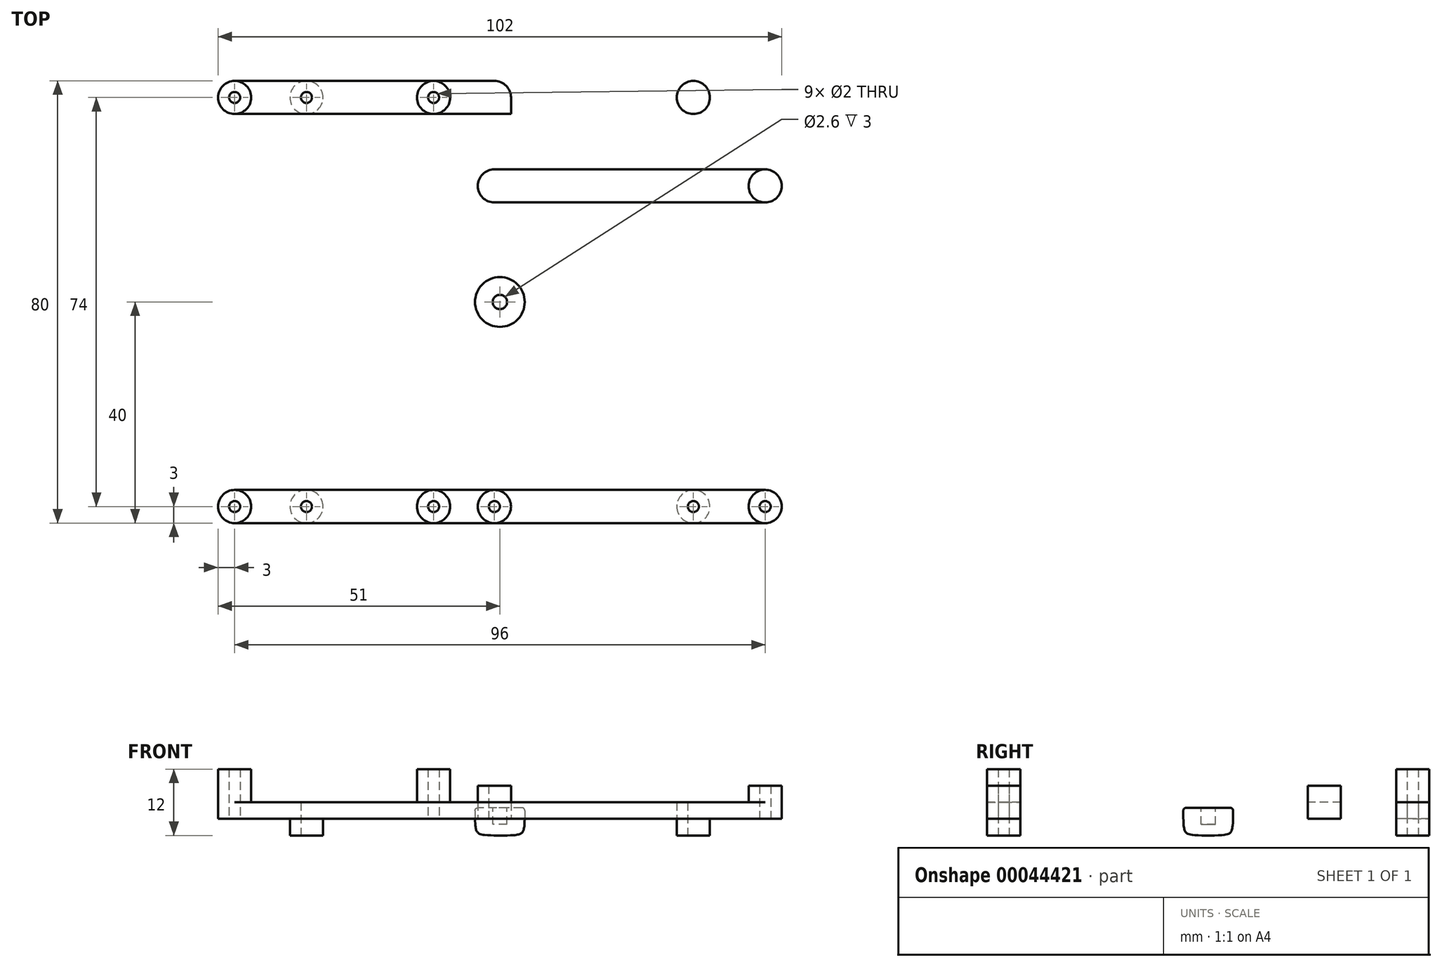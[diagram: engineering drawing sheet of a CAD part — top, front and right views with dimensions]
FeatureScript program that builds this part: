
annotation { "Feature Type Name" : "Feature", "Feature Type Description" : "" }
export const myFeature = defineFeature(function(context is Context, id is Id, definition is map)
    precondition{}
    {
        {
            var Q0;
            Q0=qCreatedBy(makeId("Top.planeOp"),FACE);
            var sketch = newSketch(context, id + "F0", { "sketchPlane" : qUnion([Q0])});
            skPoint(sketch, "E0.rect.middle", {"position": v(0, 0) * mm});
            skPoint(sketch, "E1", {"position": v(-35, 37) * mm});
            skCircle(sketch, "E2", {"center": v(-35, 37) * mm, "radius": 3 * mm});
            skSolve(sketch);
        }
        {
            var Q0;
            Q0=makeQuery(id+"F0.imprint","IMPRINT",FACE,{"disambiguationData":[TD([[makeQuery(id+"F0.imprint","IMPRINT",EDGE,{"derivedFrom":sQuery(id+"F0.wireOp",EDGE,"E2")}),1.0]])]});
            extrude(context, id + "F1", {"entities" : qUnion([Q0]), "depth" : 3 * mm});
        }
        {
            var Q0;
            Q0=makeQuery(id+"F1.opExtrude","SWEPT_BODY",BODY,{"disambiguationData":[OSD([sQuery(id+"F0.wireOp",EDGE,"E2")])]});
            var Q1;
            Q1=qCreatedBy(makeId("Right.planeOp"),FACE);
            mirror(context, id + "F2", {"entities" : qUnion([Q0]), "mirrorPlane" : qUnion([Q1])});
        }
        {
            var Q0;
            Q0=makeQuery(id+"F1.opExtrude","SWEPT_BODY",BODY,{"disambiguationData":[OSD([sQuery(id+"F0.wireOp",EDGE,"E2")])]});
            var Q1;
            Q1=makeQuery(id+"F2.opPattern","COPY",BODY,{"derivedFrom":makeQuery(id+"F1.opExtrude","SWEPT_BODY",BODY,{"disambiguationData":[OSD([sQuery(id+"F0.wireOp",EDGE,"E2")])]}),"instanceName":"1"});
            var Q2;
            Q2=qCreatedBy(makeId("Front.planeOp"),FACE);
            mirror(context, id + "F3", {"entities" : qUnion([Q0, Q1]), "mirrorPlane" : qUnion([Q2])});
        }
        {
            var Q0;
            Q0=makeQuery(id+"F3.opPattern","COPY",FACE,{"derivedFrom":makeQuery(id+"F1.opExtrude","CAP_FACE",FACE,{"disambiguationData":[OSD([sQuery(id+"F0.wireOp",EDGE,"E2")])],"isStart":false}),"instanceName":"1"});
            var sketch = newSketch(context, id + "F4", { "sketchPlane" : qUnion([Q0])});
            skCircle(sketch, "E3.0", {"center": v(-35, -37) * mm, "radius": 3 * mm});
            skCircle(sketch, "E3.1", {"center": v(35, -37) * mm, "radius": 3 * mm});
            skLineSegment(sketch, "E4.bottom", {"start": v(-51, -34) * mm, "end": v(51, -34) * mm});
            skLineSegment(sketch, "E4.top", {"start": v(-51, -40) * mm, "end": v(51, -40) * mm});
            skLineSegment(sketch, "E4.left", {"start": v(-51, -34) * mm, "end": v(-51, -40) * mm});
            skLineSegment(sketch, "E4.right", {"start": v(51, -34) * mm, "end": v(51, -40) * mm});
            skPoint(sketch, "E5", {"position": v(0, -34) * mm});
            skPoint(sketch, "E6", {"position": v(-51, -37) * mm});
            skLineSegment(sketch, "E7.bottom", {"start": v(-51, 40) * mm, "end": v(51, 40) * mm});
            skLineSegment(sketch, "E7.top", {"start": v(-51, 34) * mm, "end": v(51, 34) * mm});
            skLineSegment(sketch, "E7.left", {"start": v(-51, 40) * mm, "end": v(-51, 34) * mm});
            skLineSegment(sketch, "E7.right", {"start": v(51, 40) * mm, "end": v(51, 34) * mm});
            skPoint(sketch, "E8", {"position": v(-51, 37) * mm});
            skPoint(sketch, "E9", {"position": v(0, 40) * mm});
            skCircle(sketch, "E10.0", {"center": v(-35, 37) * mm, "radius": 3 * mm});
            skLineSegment(sketch, "E11.bottom", {"start": v(-51, 40) * mm, "end": v(2, 40) * mm});
            skLineSegment(sketch, "E11.top", {"start": v(-51, 34) * mm, "end": v(2, 34) * mm});
            skLineSegment(sketch, "E11.right", {"start": v(2, 40) * mm, "end": v(2, 34) * mm});
            skLineSegment(sketch, "E12.bottom", {"start": v(2, 34) * mm, "end": v(-4, 34) * mm});
            skLineSegment(sketch, "E12.top", {"start": v(2, 24) * mm, "end": v(-4, 24) * mm});
            skLineSegment(sketch, "E12.left", {"start": v(2, 34) * mm, "end": v(2, 24) * mm});
            skLineSegment(sketch, "E12.right", {"start": v(-4, 34) * mm, "end": v(-4, 24) * mm});
            skLineSegment(sketch, "E13.bottom", {"start": v(-4, 24) * mm, "end": v(51, 24) * mm});
            skLineSegment(sketch, "E13.top", {"start": v(-4, 18) * mm, "end": v(51, 18) * mm});
            skLineSegment(sketch, "E13.left", {"start": v(-4, 24) * mm, "end": v(-4, 18) * mm});
            skLineSegment(sketch, "E13.right", {"start": v(51, 24) * mm, "end": v(51, 18) * mm});
            skLineSegment(sketch, "E14.bottom", {"start": v(32, 40) * mm, "end": v(38, 40) * mm});
            skLineSegment(sketch, "E14.top", {"start": v(32, 24) * mm, "end": v(38, 24) * mm});
            skLineSegment(sketch, "E14.left", {"start": v(32, 40) * mm, "end": v(32, 24) * mm});
            skLineSegment(sketch, "E14.right", {"start": v(38, 40) * mm, "end": v(38, 24) * mm});
            skPoint(sketch, "E15", {"position": v(35, 24) * mm});
            skCircle(sketch, "E16.0", {"center": v(35, 37) * mm, "radius": 3 * mm});
            skSolve(sketch);
        }
        {
            var Q0;
            {var subQ5=sQuery(id+"F4.wireOp",EDGE,"E11.right");Q0=makeQuery(id+"F4.imprint","IMPRINT",FACE,{"disambiguationData":[TD([[makeQuery(id+"F4.imprint","IMPRINT",EDGE,{"derivedFrom":subQ5}),-1.0]])]});}
            var Q1;
            {var subQ0=sQuery(id+"F4.wireOp",EDGE,"E10.0");var subQ1=makeQuery(id+"F4.imprint","INTERSECT",VERTEX,{"derivedFrom":[subQ0,sQuery(id+"F4.wireOp",EDGE,"E11.bottom")]});Q1=makeQuery(id+"F4.imprint","IMPRINT",FACE,{"disambiguationData":[TD([[makeQuery(id+"F4.imprint","IMPRINT",EDGE,{"disambiguationData":[TD([[subQ1,-1.0]])],"derivedFrom":subQ0}),1.0]])]});}
            var Q2;
            {var subQ5=sQuery(id+"F4.wireOp",EDGE,"E7.left");Q2=makeQuery(id+"F4.imprint","IMPRINT",FACE,{"disambiguationData":[TD([[makeQuery(id+"F4.imprint","IMPRINT",EDGE,{"derivedFrom":subQ5}),1.0]])]});}
            var Q3;
            Q3=makeQuery(id+"F4.imprint","IMPRINT",FACE,{"disambiguationData":[TD([[makeQuery(id+"F4.imprint","IMPRINT",EDGE,{"derivedFrom":sQuery(id+"F4.wireOp",EDGE,"E12.bottom")}),1.0]])]});
            var Q4;
            Q4=makeQuery(id+"F4.imprint","IMPRINT",FACE,{"disambiguationData":[TD([[makeQuery(id+"F4.imprint","IMPRINT",EDGE,{"derivedFrom":sQuery(id+"F4.wireOp",EDGE,"E13.top")}),1.0]])]});
            var Q5;
            {var subQ1=sQuery(id+"F4.wireOp",EDGE,"E14.top");Q5=makeQuery(id+"F4.imprint","IMPRINT",FACE,{"disambiguationData":[TD([[makeQuery(id+"F4.imprint","IMPRINT",EDGE,{"derivedFrom":subQ1}),1.0]])]});}
            var Q6;
            {var subQ0=sQuery(id+"F4.wireOp",EDGE,"E14.right");var subQ1=sQuery(id+"F4.wireOp",EDGE,"E7.top");var subQ2=makeQuery(id+"F4.imprint","INTERSECT",VERTEX,{"derivedFrom":[subQ1,subQ0]});Q6=makeQuery(id+"F4.imprint","IMPRINT",FACE,{"disambiguationData":[TD([[makeQuery(id+"F4.imprint","IMPRINT",EDGE,{"disambiguationData":[TD([[subQ2,1.0]])],"derivedFrom":subQ1}),1.0]])]});}
            var Q7;
            {var subQ0=sQuery(id+"F4.wireOp",EDGE,"E14.left");var subQ1=sQuery(id+"F4.wireOp",EDGE,"E7.top");var subQ2=makeQuery(id+"F4.imprint","INTERSECT",VERTEX,{"derivedFrom":[subQ1,subQ0]});Q7=makeQuery(id+"F4.imprint","IMPRINT",FACE,{"disambiguationData":[TD([[makeQuery(id+"F4.imprint","IMPRINT",EDGE,{"disambiguationData":[TD([[subQ2,-1.0]])],"derivedFrom":subQ1}),1.0]])]});}
            var Q8;
            {var subQ0=sQuery(id+"F4.wireOp",EDGE,"E16.0");var subQ1=makeQuery(id+"F4.imprint","INTERSECT",VERTEX,{"derivedFrom":[sQuery(id+"F4.wireOp",EDGE,"E14.bottom"),subQ0]});Q8=makeQuery(id+"F4.imprint","IMPRINT",FACE,{"disambiguationData":[TD([[makeQuery(id+"F4.imprint","IMPRINT",EDGE,{"disambiguationData":[TD([[subQ1,1.0]])],"derivedFrom":subQ0}),1.0]])]});}
            extrude(context, id + "F5", {"entities" : qUnion([Q0, Q1, Q2, Q3, Q4, Q5, Q6, Q7, Q8]), "operationType" : NewBodyOperationType.ADD, "depth" : 3 * mm});
        }
        {
            var Q0;
            Q0=makeQuery(id+"F5.opExtrude","SWEPT_EDGE",EDGE,{"disambiguationData":[OSD([sQuery(id+"F4.wireOp",EDGE,"E11.top"),sQuery(id+"F4.wireOp",EDGE,"E7.left")])]});
            var Q1;
            Q1=makeQuery(id+"F5.opExtrude","SWEPT_EDGE",EDGE,{"disambiguationData":[OSD([sQuery(id+"F4.wireOp",EDGE,"E11.bottom"),sQuery(id+"F4.wireOp",EDGE,"E7.left")])]});
            var Q2;
            Q2=makeQuery(id+"F5.opExtrude","SWEPT_EDGE",EDGE,{"disambiguationData":[OSD([sQuery(id+"F4.wireOp",EDGE,"E7.bottom"),sQuery(id+"F4.wireOp",EDGE,"E11.bottom"),sQuery(id+"F4.wireOp",EDGE,"E11.right")])]});
            var Q3;
            Q3=makeQuery(id+"F5.opExtrude","SWEPT_EDGE",EDGE,{"disambiguationData":[OSD([sQuery(id+"F4.wireOp",EDGE,"E13.top"),sQuery(id+"F4.wireOp",EDGE,"E13.left")])]});
            var Q4;
            Q4=makeQuery(id+"F5.opExtrude","SWEPT_EDGE",EDGE,{"disambiguationData":[OSD([sQuery(id+"F4.wireOp",EDGE,"E13.top"),sQuery(id+"F4.wireOp",EDGE,"E13.right")])]});
            var Q5;
            Q5=makeQuery(id+"F5.opExtrude","SWEPT_EDGE",EDGE,{"disambiguationData":[OSD([sQuery(id+"F4.wireOp",EDGE,"E13.bottom"),sQuery(id+"F4.wireOp",EDGE,"E13.right")])]});
            var Q6;
            Q6=makeQuery(id+"F5.opExtrude","SWEPT_EDGE",EDGE,{"disambiguationData":[OSD([sQuery(id+"F4.wireOp",EDGE,"E13.bottom"),sQuery(id+"F4.wireOp",EDGE,"E14.top"),sQuery(id+"F4.wireOp",EDGE,"E14.right")])]});
            var Q7;
            Q7=makeQuery(id+"F5.opExtrude","SWEPT_EDGE",EDGE,{"disambiguationData":[OSD([sQuery(id+"F4.wireOp",EDGE,"E12.left"),sQuery(id+"F4.wireOp",EDGE,"E13.bottom")])]});
            var Q8;
            Q8=makeQuery(id+"F5.opExtrude","SWEPT_EDGE",EDGE,{"disambiguationData":[OSD([sQuery(id+"F4.wireOp",EDGE,"E13.bottom"),sQuery(id+"F4.wireOp",EDGE,"E14.top"),sQuery(id+"F4.wireOp",EDGE,"E14.left")])]});
            var Q9;
            Q9=makeQuery(id+"F5.opExtrude","SWEPT_EDGE",EDGE,{"disambiguationData":[OSD([sQuery(id+"F4.wireOp",EDGE,"E11.top"),sQuery(id+"F4.wireOp",EDGE,"E12.bottom"),sQuery(id+"F4.wireOp",EDGE,"E12.right")])]});
            fillet(context, id + "F6", {"entities" : qUnion([Q0, Q1, Q2, Q3, Q4, Q5, Q6, Q7, Q8, Q9]), "radius" : 3 * mm, "tangentPropagation" : true, "allowEdgeOverflow" : false});
        }
        {
            var Q0;
            {var subQ0=sQuery(id+"F4.wireOp",EDGE,"E4.bottom");var subQ1=sQuery(id+"F4.wireOp",EDGE,"E3.0");var subQ2=makeQuery(id+"F4.imprint","INTERSECT",VERTEX,{"derivedFrom":[subQ1,subQ0]});Q0=makeQuery(id+"F4.imprint","IMPRINT",FACE,{"disambiguationData":[TD([[makeQuery(id+"F4.imprint","IMPRINT",EDGE,{"disambiguationData":[TD([[subQ2,-1.0]])],"derivedFrom":subQ1}),1.0]])]});}
            var Q1;
            Q1=makeQuery(id+"F4.imprint","IMPRINT",FACE,{"disambiguationData":[TD([[makeQuery(id+"F4.imprint","IMPRINT",EDGE,{"derivedFrom":makeQuery(id+"F3.opPattern","COPY",EDGE,{"derivedFrom":makeQuery(id+"Fms3Rmutws8Ll0A_1.hole-0.boolean.opBoolean","INTERSECT",EDGE,{"derivedFrom":[makeQuery(id+"F1.opExtrude","CAP_FACE",FACE,{"disambiguationData":[OSD([sQuery(id+"F0.wireOp",EDGE,"E2")])],"isStart":false}),makeQuery(id+"Fms3Rmutws8Ll0A_1.hole-0.opRevolve","SWEPT_FACE",FACE,{"disambiguationData":[OSD([sQuery(id+"Fms3Rmutws8Ll0A_1.hole-0.sketch.wireOp",EDGE,"core_line_2")])]})]}),"instanceName":"1"})}),-1.0]])]});
            var Q2;
            Q2=makeQuery(id+"F4.imprint","IMPRINT",FACE,{"disambiguationData":[TD([[makeQuery(id+"F4.imprint","IMPRINT",EDGE,{"derivedFrom":makeQuery(id+"F3.opPattern","COPY",EDGE,{"derivedFrom":makeQuery(id+"Fms3Rmutws8Ll0A_1.hole-0.boolean.opBoolean","INTERSECT",EDGE,{"derivedFrom":[makeQuery(id+"F1.opExtrude","CAP_FACE",FACE,{"disambiguationData":[OSD([sQuery(id+"F0.wireOp",EDGE,"E2")])],"isStart":false}),makeQuery(id+"Fms3Rmutws8Ll0A_1.hole-0.opRevolve","SWEPT_FACE",FACE,{"disambiguationData":[OSD([sQuery(id+"Fms3Rmutws8Ll0A_1.hole-0.sketch.wireOp",EDGE,"core_line_2")])]})]}),"instanceName":"1"})}),1.0]])]});
            var Q3;
            {var subQ5=sQuery(id+"F4.wireOp",EDGE,"E4.left");Q3=makeQuery(id+"F4.imprint","IMPRINT",FACE,{"disambiguationData":[TD([[makeQuery(id+"F4.imprint","IMPRINT",EDGE,{"derivedFrom":subQ5}),1.0]])]});}
            var Q4;
            {var subQ5=sQuery(id+"F4.wireOp",EDGE,"E4.right");Q4=makeQuery(id+"F4.imprint","IMPRINT",FACE,{"disambiguationData":[TD([[makeQuery(id+"F4.imprint","IMPRINT",EDGE,{"derivedFrom":subQ5}),-1.0]])]});}
            var Q5;
            {var subQ0=sQuery(id+"F4.wireOp",EDGE,"E3.1");var subQ1=makeQuery(id+"F4.imprint","INTERSECT",VERTEX,{"derivedFrom":[subQ0,sQuery(id+"F4.wireOp",EDGE,"E4.bottom")]});Q5=makeQuery(id+"F4.imprint","IMPRINT",FACE,{"disambiguationData":[TD([[makeQuery(id+"F4.imprint","IMPRINT",EDGE,{"disambiguationData":[TD([[subQ1,-1.0]])],"derivedFrom":subQ0}),1.0]])]});}
            var Q6;
            {var subQ0=sQuery(id+"F4.wireOp",EDGE,"E3.0");var subQ1=makeQuery(id+"F4.imprint","INTERSECT",VERTEX,{"derivedFrom":[subQ0,sQuery(id+"F4.wireOp",EDGE,"E4.bottom")]});Q6=makeQuery(id+"F4.imprint","IMPRINT",FACE,{"disambiguationData":[TD([[makeQuery(id+"F4.imprint","IMPRINT",EDGE,{"disambiguationData":[TD([[subQ1,1.0]])],"derivedFrom":subQ0}),-1.0]])]});}
            extrude(context, id + "F7", {"entities" : qUnion([Q0, Q1, Q2, Q3, Q4, Q5, Q6]), "operationType" : NewBodyOperationType.ADD, "depth" : 3 * mm});
        }
        {
            var Q0;
            Q0=makeQuery(id+"F7.opExtrude","SWEPT_EDGE",EDGE,{"disambiguationData":[OSD([sQuery(id+"F4.wireOp",EDGE,"E4.bottom"),sQuery(id+"F4.wireOp",EDGE,"E4.left")])]});
            var Q1;
            Q1=makeQuery(id+"F7.opExtrude","SWEPT_EDGE",EDGE,{"disambiguationData":[OSD([sQuery(id+"F4.wireOp",EDGE,"E4.top"),sQuery(id+"F4.wireOp",EDGE,"E4.left")])]});
            var Q2;
            Q2=makeQuery(id+"F7.opExtrude","SWEPT_EDGE",EDGE,{"disambiguationData":[OSD([sQuery(id+"F4.wireOp",EDGE,"E4.bottom"),sQuery(id+"F4.wireOp",EDGE,"E4.right")])]});
            var Q3;
            Q3=makeQuery(id+"F7.opExtrude","SWEPT_EDGE",EDGE,{"disambiguationData":[OSD([sQuery(id+"F4.wireOp",EDGE,"E4.top"),sQuery(id+"F4.wireOp",EDGE,"E4.right")])]});
            fillet(context, id + "F8", {"entities" : qUnion([Q0, Q1, Q2, Q3]), "radius" : 3 * mm, "tangentPropagation" : true, "allowEdgeOverflow" : false});
        }
        {
            var Q0;
            Q0=makeQuery(id+"F7.opExtrude","CAP_FACE",FACE,{"disambiguationData":[OSD([sQuery(id+"F4.wireOp",EDGE,"E4.bottom"),sQuery(id+"F4.wireOp",EDGE,"E4.top"),sQuery(id+"F4.wireOp",EDGE,"E4.left"),sQuery(id+"F4.wireOp",EDGE,"E4.right")])],"isStart":false});
            var sketch = newSketch(context, id + "F9", { "sketchPlane" : qUnion([Q0])});
            skArc(sketch, "E17.0", {"start": v(-48, -34) * mm, "mid": v(-51, -37) * mm, "end": v(-48, -40) * mm});
            skCircle(sketch, "E18", {"center": v(-48, -37) * mm, "radius": 3 * mm});
            skCircle(sketch, "E19", {"center": v(-12, -37) * mm, "radius": 3 * mm});
            skArc(sketch, "E20.0", {"start": v(48, -40) * mm, "mid": v(51, -37) * mm, "end": v(48, -34) * mm});
            skCircle(sketch, "E21", {"center": v(48, -37) * mm, "radius": 3 * mm});
            skCircle(sketch, "E22", {"center": v(-1, -37) * mm, "radius": 3 * mm});
            skCircle(sketch, "E23.0", {"center": v(-35, -37) * mm, "radius": 3 * mm});
            skCircle(sketch, "E23.1", {"center": v(35, -37) * mm, "radius": 3 * mm});
            skSolve(sketch);
        }
        {
            var Q0;
            {var subQ0=sQuery(id+"F9.wireOp",EDGE,"E19");var subQ1=makeQuery(id+"F9.imprint","INTERSECT",VERTEX,{"derivedFrom":[makeQuery(id+"F7.opExtrude","CAP_EDGE",EDGE,{"disambiguationData":[OSD([sQuery(id+"F4.wireOp",EDGE,"E4.bottom")])],"isStart":false}),subQ0]});Q0=makeQuery(id+"F9.imprint","IMPRINT",FACE,{"disambiguationData":[TD([[makeQuery(id+"F9.imprint","IMPRINT",EDGE,{"disambiguationData":[TD([[subQ1,-1.0]])],"derivedFrom":subQ0}),1.0]])]});}
            var Q1;
            {var subQ0=sQuery(id+"F9.wireOp",EDGE,"E18");var subQ1=makeQuery(id+"F9.imprint","INTERSECT",VERTEX,{"derivedFrom":[makeQuery(id+"F7.opExtrude","CAP_EDGE",EDGE,{"disambiguationData":[OSD([sQuery(id+"F4.wireOp",EDGE,"E4.bottom")])],"isStart":false}),subQ0]});Q1=makeQuery(id+"F9.imprint","IMPRINT",FACE,{"disambiguationData":[TD([[makeQuery(id+"F9.imprint","IMPRINT",EDGE,{"disambiguationData":[TD([[subQ1,-1.0]])],"derivedFrom":subQ0}),1.0]])]});}
            extrude(context, id + "F10", {"entities" : qUnion([Q0, Q1]), "operationType" : NewBodyOperationType.ADD, "depth" : 6 * mm});
        }
        {
            var Q0;
            {var subQ0=sQuery(id+"F9.wireOp",EDGE,"E22");var subQ1=makeQuery(id+"F9.imprint","INTERSECT",VERTEX,{"derivedFrom":[makeQuery(id+"F7.opExtrude","CAP_EDGE",EDGE,{"disambiguationData":[OSD([sQuery(id+"F4.wireOp",EDGE,"E4.bottom")])],"isStart":false}),subQ0]});Q0=makeQuery(id+"F9.imprint","IMPRINT",FACE,{"disambiguationData":[TD([[makeQuery(id+"F9.imprint","IMPRINT",EDGE,{"disambiguationData":[TD([[subQ1,-1.0]])],"derivedFrom":subQ0}),1.0]])]});}
            var Q1;
            {var subQ0=sQuery(id+"F9.wireOp",EDGE,"E21");var subQ1=makeQuery(id+"F9.imprint","INTERSECT",VERTEX,{"derivedFrom":[makeQuery(id+"F7.opExtrude","CAP_EDGE",EDGE,{"disambiguationData":[OSD([sQuery(id+"F4.wireOp",EDGE,"E4.bottom")])],"isStart":false}),subQ0]});Q1=makeQuery(id+"F9.imprint","IMPRINT",FACE,{"disambiguationData":[TD([[makeQuery(id+"F9.imprint","IMPRINT",EDGE,{"disambiguationData":[TD([[subQ1,-1.0]])],"derivedFrom":subQ0}),1.0]])]});}
            extrude(context, id + "F11", {"entities" : qUnion([Q0, Q1]), "operationType" : NewBodyOperationType.ADD, "depth" : 3 * mm});
        }
        {
            var Q0;
            Q0=makeQuery(id+"F10.opExtrude","CAP_FACE",FACE,{"disambiguationData":[OSD([sQuery(id+"F9.wireOp",EDGE,"E18")])],"isStart":false});
            var sketch = newSketch(context, id + "F12", { "sketchPlane" : qUnion([Q0])});
            skCircle(sketch, "E24.0", {"center": v(-48, -37) * mm, "radius": 3 * mm});
            skCircle(sketch, "E24.1", {"center": v(-12, -37) * mm, "radius": 3 * mm});
            skCircle(sketch, "E24.2", {"center": v(-1, -37) * mm, "radius": 3 * mm});
            skCircle(sketch, "E24.3", {"center": v(48, -37) * mm, "radius": 3 * mm});
            skSolve(sketch);
        }
        {
            var Q0;
            Q0=sQuery(id+"F12.wireOp",VERTEX,"E24.0.center");
            var Q1;
            Q1=sQuery(id+"F12.wireOp",VERTEX,"E24.1.center");
            var Q2;
            Q2=sQuery(id+"F12.wireOp",VERTEX,"E24.2.center");
            var Q3;
            Q3=sQuery(id+"F12.wireOp",VERTEX,"E24.3.center");
            var Q4;
            Q4=makeQuery(id+"F3.opPattern","COPY",BODY,{"derivedFrom":makeQuery(id+"F1.opExtrude","SWEPT_BODY",BODY,{"disambiguationData":[OSD([sQuery(id+"F0.wireOp",EDGE,"E2")])]}),"instanceName":"1"});
            hole(context, id + "F13", {"style" : HoleStyle.SIMPLE, "holeDiameter" : 2 * mm, "endStyle" : HoleEndStyle.THROUGH, "locations" : qUnion([Q0, Q1, Q2, Q3]), "scope" : qUnion([Q4])});
        }
        {
            var Q0;
            Q0=makeQuery(id+"F5.opExtrude","CAP_FACE",FACE,{"disambiguationData":[OSD([sQuery(id+"F4.wireOp",EDGE,"E11.bottom"),sQuery(id+"F4.wireOp",EDGE,"E11.top"),sQuery(id+"F4.wireOp",EDGE,"E7.left"),sQuery(id+"F4.wireOp",EDGE,"E11.right"),sQuery(id+"F4.wireOp",EDGE,"E12.left"),sQuery(id+"F4.wireOp",EDGE,"E12.right"),sQuery(id+"F4.wireOp",EDGE,"E13.bottom"),sQuery(id+"F4.wireOp",EDGE,"E13.top"),sQuery(id+"F4.wireOp",EDGE,"E13.left"),sQuery(id+"F4.wireOp",EDGE,"E13.right"),sQuery(id+"F4.wireOp",EDGE,"E14.left"),sQuery(id+"F4.wireOp",EDGE,"E14.right"),sQuery(id+"F4.wireOp",EDGE,"E16.0")])],"isStart":false});
            var sketch = newSketch(context, id + "F14", { "sketchPlane" : qUnion([Q0])});
            skArc(sketch, "E25.0", {"start": v(-4, 21) * mm, "mid": v(-3.12, 18.88) * mm, "end": v(-1, 18) * mm});
            skArc(sketch, "E25.1", {"start": v(48, 18) * mm, "mid": v(51, 21) * mm, "end": v(48, 24) * mm});
            skCircle(sketch, "E26", {"center": v(-1, 21) * mm, "radius": 3 * mm});
            skCircle(sketch, "E27", {"center": v(48, 21) * mm, "radius": 3 * mm});
            skArc(sketch, "E28.0", {"start": v(-48, 40) * mm, "mid": v(-51, 37) * mm, "end": v(-48, 34) * mm});
            skCircle(sketch, "E29", {"center": v(-48, 37) * mm, "radius": 3 * mm});
            skCircle(sketch, "E30", {"center": v(-12, 37) * mm, "radius": 3 * mm});
            skCircle(sketch, "E31.0", {"center": v(-35, 37) * mm, "radius": 3 * mm});
            skCircle(sketch, "E31.1", {"center": v(35, 37) * mm, "radius": 3 * mm});
            skSolve(sketch);
        }
        {
            var Q0;
            Q0=sQuery(id+"F9.wireOp",VERTEX,"E23.0.center");
            var Q1;
            Q1=sQuery(id+"F9.wireOp",VERTEX,"E23.1.center");
            var Q2;
            Q2=makeQuery(id+"F3.opPattern","COPY",BODY,{"derivedFrom":makeQuery(id+"F1.opExtrude","SWEPT_BODY",BODY,{"disambiguationData":[OSD([sQuery(id+"F0.wireOp",EDGE,"E2")])]}),"instanceName":"1"});
            hole(context, id + "F15", {"style" : HoleStyle.SIMPLE, "holeDiameter" : 2 * mm, "endStyle" : HoleEndStyle.THROUGH, "locations" : qUnion([Q0, Q1]), "scope" : qUnion([Q2])});
        }
        {
            var Q0;
            {var subQ0=sQuery(id+"F14.wireOp",EDGE,"E26");var subQ2=makeQuery(id+"F14.imprint","INTERSECT",VERTEX,{"derivedFrom":[makeQuery(id+"F5.opExtrude","CAP_EDGE",EDGE,{"disambiguationData":[OSD([sQuery(id+"F4.wireOp",EDGE,"E13.top")])],"isStart":false}),subQ0]});Q0=makeQuery(id+"F14.imprint","IMPRINT",FACE,{"disambiguationData":[TD([[makeQuery(id+"F14.imprint","IMPRINT",EDGE,{"disambiguationData":[TD([[subQ2,1.0]])],"derivedFrom":subQ0}),1.0]])]});}
            var Q1;
            {var subQ0=sQuery(id+"F14.wireOp",EDGE,"E27");var subQ3=makeQuery(id+"F14.imprint","INTERSECT",VERTEX,{"derivedFrom":[makeQuery(id+"F5.opExtrude","CAP_EDGE",EDGE,{"disambiguationData":[OSD([sQuery(id+"F4.wireOp",EDGE,"E13.top")])],"isStart":false}),subQ0]});Q1=makeQuery(id+"F14.imprint","IMPRINT",FACE,{"disambiguationData":[TD([[makeQuery(id+"F14.imprint","IMPRINT",EDGE,{"disambiguationData":[TD([[subQ3,1.0]])],"derivedFrom":subQ0}),1.0]])]});}
            extrude(context, id + "F16", {"entities" : qUnion([Q0, Q1]), "operationType" : NewBodyOperationType.ADD, "depth" : 3 * mm});
        }
        {
            var Q0;
            {var subQ0=sQuery(id+"F14.wireOp",EDGE,"E29");var subQ1=makeQuery(id+"F14.imprint","INTERSECT",VERTEX,{"derivedFrom":[makeQuery(id+"F5.opExtrude","CAP_EDGE",EDGE,{"disambiguationData":[OSD([sQuery(id+"F4.wireOp",EDGE,"E11.bottom")])],"isStart":false}),subQ0]});Q0=makeQuery(id+"F14.imprint","IMPRINT",FACE,{"disambiguationData":[TD([[makeQuery(id+"F14.imprint","IMPRINT",EDGE,{"disambiguationData":[TD([[subQ1,-1.0]])],"derivedFrom":subQ0}),1.0]])]});}
            var Q1;
            {var subQ0=sQuery(id+"F14.wireOp",EDGE,"E30");var subQ1=makeQuery(id+"F14.imprint","INTERSECT",VERTEX,{"derivedFrom":[makeQuery(id+"F5.opExtrude","CAP_EDGE",EDGE,{"disambiguationData":[OSD([sQuery(id+"F4.wireOp",EDGE,"E11.bottom")])],"isStart":false}),subQ0]});Q1=makeQuery(id+"F14.imprint","IMPRINT",FACE,{"disambiguationData":[TD([[makeQuery(id+"F14.imprint","IMPRINT",EDGE,{"disambiguationData":[TD([[subQ1,-1.0]])],"derivedFrom":subQ0}),1.0]])]});}
            extrude(context, id + "F17", {"entities" : qUnion([Q0, Q1]), "operationType" : NewBodyOperationType.ADD, "depth" : 6 * mm});
        }
        {
            var Q0;
            Q0=makeQuery(id+"F17.opExtrude","CAP_FACE",FACE,{"disambiguationData":[OSD([sQuery(id+"F14.wireOp",EDGE,"E29")])],"isStart":false});
            var sketch = newSketch(context, id + "F18", { "sketchPlane" : qUnion([Q0])});
            skCircle(sketch, "E32.0", {"center": v(-48, 37) * mm, "radius": 3 * mm});
            skCircle(sketch, "E32.1", {"center": v(-12, 37) * mm, "radius": 3 * mm});
            skCircle(sketch, "E32.2", {"center": v(-1, 21) * mm, "radius": 3 * mm});
            skCircle(sketch, "E32.3", {"center": v(48, 21) * mm, "radius": 3 * mm});
            skSolve(sketch);
        }
        {
            var Q0;
            Q0=sQuery(id+"F18.wireOp",VERTEX,"E32.0.center");
            var Q1;
            Q1=sQuery(id+"F18.wireOp",VERTEX,"E32.1.center");
            var Q2;
            Q2=sQuery(id+"F18.wireOp",VERTEX,"E32.2.center");
            var Q3;
            Q3=sQuery(id+"F18.wireOp",VERTEX,"E32.3.center");
            var Q4;
            Q4=makeQuery(id+"F1.opExtrude","SWEPT_BODY",BODY,{"disambiguationData":[OSD([sQuery(id+"F0.wireOp",EDGE,"E2")])]});
            hole(context, id + "F19", {"style" : HoleStyle.SIMPLE, "holeDiameter" : 2 * mm, "endStyle" : HoleEndStyle.THROUGH, "locations" : qUnion([Q0, Q1, Q2, Q3]), "scope" : qUnion([Q4])});
        }
        {
            var Q0;
            Q0=sQuery(id+"F14.wireOp",VERTEX,"E31.0.center");
            var Q1;
            Q1=sQuery(id+"F14.wireOp",VERTEX,"E31.1.center");
            var Q2;
            Q2=makeQuery(id+"F1.opExtrude","SWEPT_BODY",BODY,{"disambiguationData":[OSD([sQuery(id+"F0.wireOp",EDGE,"E2")])]});
            hole(context, id + "F20", {"style" : HoleStyle.SIMPLE, "holeDiameter" : 2 * mm, "endStyle" : HoleEndStyle.THROUGH, "locations" : qUnion([Q0, Q1]), "scope" : qUnion([Q2])});
        }
        {
            var Q0;
            Q0=qCreatedBy(makeId("Top.planeOp"),FACE);
            var sketch = newSketch(context, id + "F21", { "sketchPlane" : qUnion([Q0])});
            skCircle(sketch, "E33", {"center": v(0, 0) * mm, "radius": 4.5 * mm});
            skSolve(sketch);
        }
        {
            var Q0;
            Q0=makeQuery(id+"F21.imprint","IMPRINT",FACE,{"disambiguationData":[TD([[makeQuery(id+"F21.imprint","IMPRINT",EDGE,{"derivedFrom":sQuery(id+"F21.wireOp",EDGE,"E33")}),1.0]])]});
            extrude(context, id + "F22", {"entities" : qUnion([Q0]), "depth" : 5 * mm});
        }
        {
            var Q0;
            Q0=makeQuery(id+"F22.opExtrude","CAP_FACE",FACE,{"disambiguationData":[OSD([sQuery(id+"F21.wireOp",EDGE,"E33")])],"isStart":false});
            var sketch = newSketch(context, id + "F23", { "sketchPlane" : qUnion([Q0])});
            skCircle(sketch, "E34.0", {"center": v(0, 0) * mm, "radius": 4.5 * mm});
            skCircle(sketch, "E35", {"center": v(0, 0) * mm, "radius": 1.3 * mm});
            skSolve(sketch);
        }
        {
            var Q0;
            Q0=makeQuery(id+"F23.imprint","IMPRINT",FACE,{"disambiguationData":[TD([[makeQuery(id+"F23.imprint","IMPRINT",EDGE,{"derivedFrom":sQuery(id+"F23.wireOp",EDGE,"E35")}),1.0]])]});
            extrude(context, id + "F24", {"entities" : qUnion([Q0]), "operationType" : NewBodyOperationType.REMOVE, "oppositeDirection" : true, "depth" : 3 * mm});
        }
        {
            var Q0;
            Q0=makeQuery(id+"F22.opExtrude","CAP_EDGE",EDGE,{"disambiguationData":[OSD([sQuery(id+"F21.wireOp",EDGE,"E33")])],"isStart":true});
            fillet(context, id + "F25", {"entities" : qUnion([Q0]), "radius" : 4 * mm, "tangentPropagation" : true, "rho" : 0.75, "crossSection" : FilletCrossSection.CONIC, "allowEdgeOverflow" : false});
        }
        {
            var Q0;
            Q0=makeQuery(id+"F24.boolean.opBoolean","COPY",EDGE,{"derivedFrom":makeQuery(id+"F24.opExtrude","CAP_EDGE",EDGE,{"disambiguationData":[OSD([sQuery(id+"F23.wireOp",EDGE,"E35")])],"isStart":true})});
            var Q1;
            Q1=makeQuery(id+"F22.opExtrude","CAP_EDGE",EDGE,{"disambiguationData":[OSD([sQuery(id+"F21.wireOp",EDGE,"E33")])],"isStart":false});
            fillet(context, id + "F26", {"entities" : qUnion([Q0, Q1]), "radius" : 0.5 * mm, "tangentPropagation" : true, "allowEdgeOverflow" : false});
        }
    });
